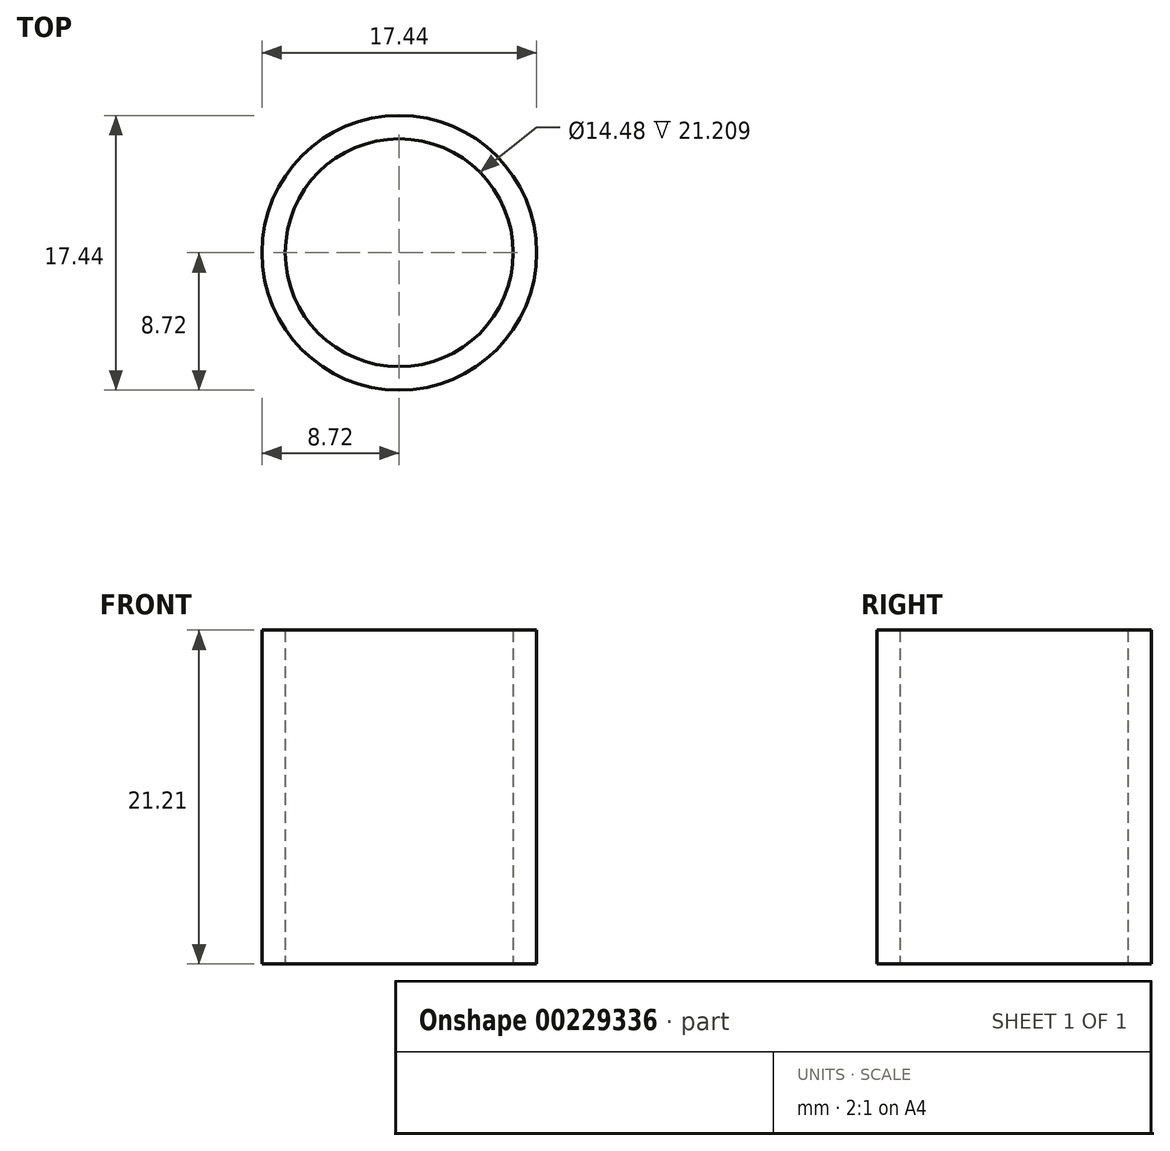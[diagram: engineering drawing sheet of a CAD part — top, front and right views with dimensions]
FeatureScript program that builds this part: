
annotation { "Feature Type Name" : "Feature", "Feature Type Description" : "" }
export const myFeature = defineFeature(function(context is Context, id is Id, definition is map)
    precondition{}
    {
        {
            var Q0;
            Q0=qCreatedBy(makeId("Right.planeOp"),FACE);
            var sketch = newSketch(context, id + "F0", { "sketchPlane" : qUnion([Q0])});
            skLineSegment(sketch, "E0", {"start": v(0, 0) * mm, "end": v(0, 21.2) * mm});
            skLineSegment(sketch, "E1", {"start": v(8.72, 0) * mm, "end": v(8.72, 21.2) * mm});
            skLineSegment(sketch, "E2", {"start": v(7.24, 0) * mm, "end": v(7.24, 21.2) * mm});
            skLineSegment(sketch, "E3", {"start": v(7.24, 21.2) * mm, "end": v(8.72, 21.2) * mm});
            skLineSegment(sketch, "E4", {"start": v(8.72, 0) * mm, "end": v(7.24, 0) * mm});
            skSolve(sketch);
        }
        {
            var Q0;
            Q0=makeQuery(id+"F0.imprint","IMPRINT",FACE,{"disambiguationData":[TD([[makeQuery(id+"F0.imprint","IMPRINT",EDGE,{"derivedFrom":sQuery(id+"F0.wireOp",EDGE,"E1")}),1.0]])]});
            var Q1;
            Q1=sQuery(id+"F0.wireOp",EDGE,"E0");
            revolve(context, id + "F1", {"entities" : qUnion([Q0]), "axis" : qUnion([Q1]), "revolveType" : RevolveType.FULL});
        }
    });
